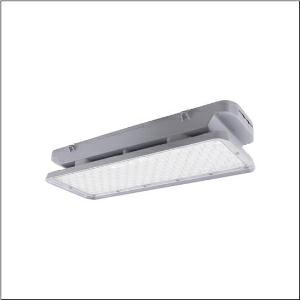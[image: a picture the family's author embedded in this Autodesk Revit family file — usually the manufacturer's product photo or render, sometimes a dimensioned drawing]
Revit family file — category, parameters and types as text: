
# Revit family: highbay_21-s_51hk41da4gca
name_source: partatom
category: Lighting Fixtures
units: mm (PartAtom-declared; Revit-internal decimal feet)

## family parameters
Cut with Voids When Loaded = No
Host = Face
Light Source = No
Part Type = Normal
Room Calculation Point = No
Round Connector Dimension = Use Diameter
Shared = No

## types (1)
- Highbay 21-S (1 x LED, 13400 lm, 75 W, 4000K)
    Apparent Load = 75 VA
    CIE Flux Codes = 87 97 99 100 100
    Color Rendering = 80
    Color Temperature = 4000K
    Default Elevation = 1800 mm
    Description = Highbay 21-S, LED high bay luminaire, primary light control with lens, of PC, light emission: direct distribution, primary light characteristic: symmetric, installation type: suspended mounting, surface-mounted, LED, rated luminous flux: 13.400lm, luminous efficacy: 180lm/W, light colour: 840, colour temperature: 4000K, with terminal, 5-pole, max. 2.5mm², mains connection: 220..240V, AC, 50Hz, rated input power: 75W, housing, of diecast aluminium, coated, grey, length: 471mm, width: 172mm, height: 87mm, protection rating (complete): IP66, insulation class (complete): insulation class I (protective earthing), certification: CE, ENEC, UKCA, protection symbol: D, impact resistance: IK08, permissible operating ambient temperature: -30..+60°C, corresponds to IFS (International Featured Standards) requirements for safety and quality in the food industry, LABS conformity tested according to VDMA 24364:2018-05, packaging unit: 1 piece
    Height = 89 mm
    Lamp = 1 x LED
    Lamp Light Flux = 13400 lm
    Lamp Power = 75 W
    Lamp count = 1
    Length = 471 mm
    Luminous efficacy = 179 lm/W
    Manufacturer = Siteco
    ModVariant = No
    Model = 51HK41DA4GCA
    Mounting Place = Ceiling
    Mounting Type = Pendant
    Number of Poles = 1
    OnlyDefault = Yes
    Power Factor = 1
    Product Name = Highbay 21-S
    Product group = LED high bay luminaire
    ProductGroupID = 903
    Protection Class = Protection class I
    Protection Degree = IP 66
    RLX_Detail_Level = 1
    RLX_Emergency_Light_Flux = 0 lm
    RLX_Emergency_Type = 0
    RLX_Emergency_Type_DB = No
    RlxData = <blob elided: 21441 chars, md5=1cf40d4a>
    Socket = socket
    Standby Power = 0 W
    System Light Flux = 13400 lm
    System Power = 75 W
    Type Comments = Product without accessories
    Type Image = l_1276526.jpg
    URL = http://relux.com
    VarID = ---
    Voltage = 0 V
    Weight = 0.00 kg
    Width = 172 mm

## geometry (parser evidence)
native form markers: Blend x4, Sweep x12
no freeform markers — native parametric forms only
